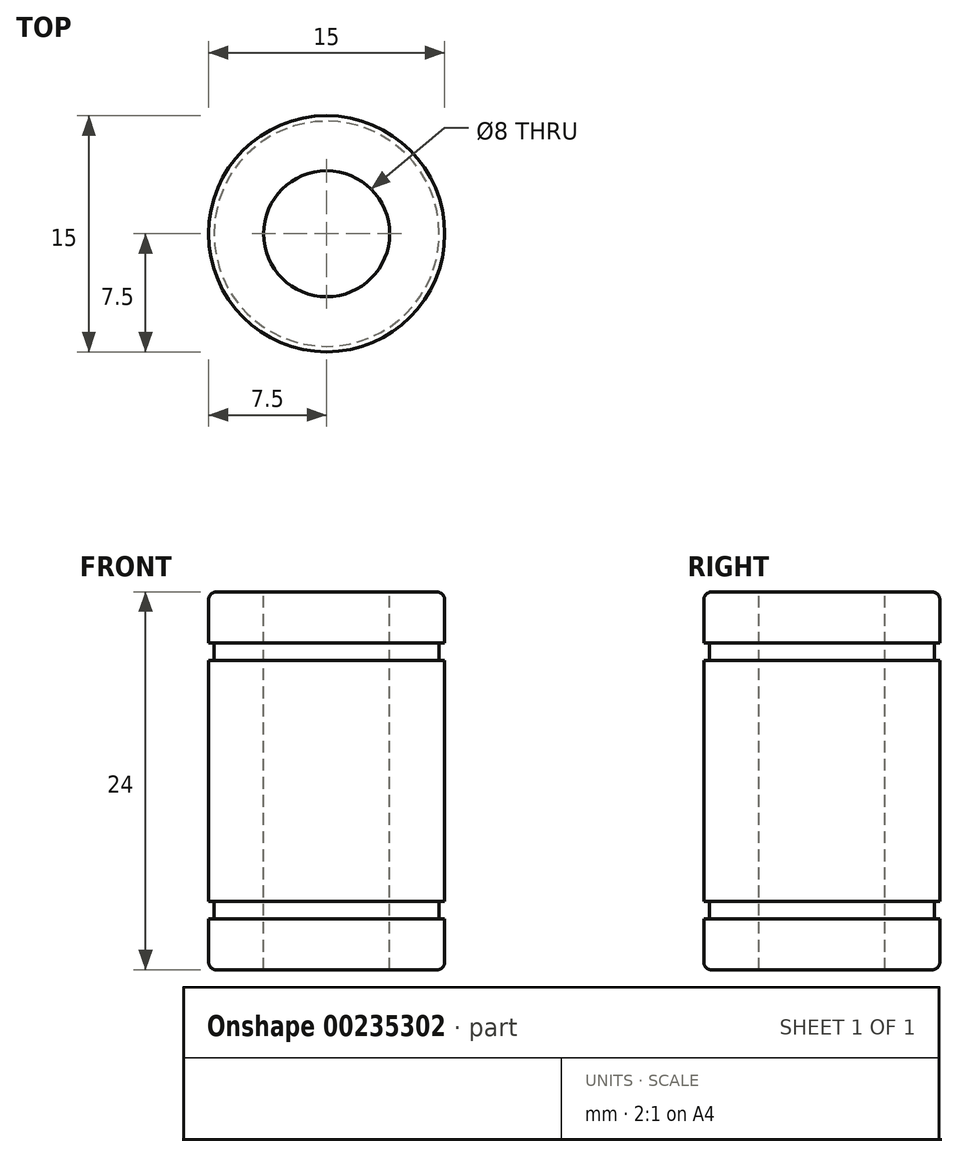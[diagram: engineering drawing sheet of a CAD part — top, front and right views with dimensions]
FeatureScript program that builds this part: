
annotation { "Feature Type Name" : "Feature", "Feature Type Description" : "" }
export const myFeature = defineFeature(function(context is Context, id is Id, definition is map)
    precondition{}
    {
        {
            var Q0;
            Q0=qCreatedBy(makeId("Front.planeOp"),FACE);
            var sketch = newSketch(context, id + "F0", { "sketchPlane" : qUnion([Q0])});
            skLineSegment(sketch, "E0", {"start": v(0, 0) * mm, "end": v(0, 24) * mm});
            skLineSegment(sketch, "E1", {"start": v(0, 24) * mm, "end": v(-7.5, 24) * mm});
            skLineSegment(sketch, "E2", {"start": v(-7.5, 24) * mm, "end": v(-7.5, 20.75) * mm});
            skLineSegment(sketch, "E3", {"start": v(-7.5, 20.75) * mm, "end": v(-7.15, 20.75) * mm});
            skLineSegment(sketch, "E4", {"start": v(-7.15, 20.75) * mm, "end": v(-7.15, 19.65) * mm});
            skLineSegment(sketch, "E5", {"start": v(-7.15, 19.65) * mm, "end": v(-7.5, 19.65) * mm});
            skLineSegment(sketch, "E6", {"start": v(-7.5, 3.25) * mm, "end": v(-7.15, 3.25) * mm});
            skLineSegment(sketch, "E7", {"start": v(-7.15, 4.35) * mm, "end": v(-7.15, 3.25) * mm});
            skLineSegment(sketch, "E8", {"start": v(-7.15, 4.35) * mm, "end": v(-7.5, 4.35) * mm});
            skLineSegment(sketch, "E9", {"start": v(-7.5, 0) * mm, "end": v(0, 0) * mm});
            skLineSegment(sketch, "E10", {"start": v(-7.5, 3.25) * mm, "end": v(-7.5, 0) * mm});
            skLineSegment(sketch, "E11", {"start": v(-7.5, 19.65) * mm, "end": v(-7.5, 4.35) * mm});
            skSolve(sketch);
        }
        {
            var Q0;
            Q0=makeQuery(id+"F0.imprint","IMPRINT",FACE,{"disambiguationData":[TD([[makeQuery(id+"F0.imprint","IMPRINT",EDGE,{"derivedFrom":sQuery(id+"F0.wireOp",EDGE,"E0")}),1.0]])]});
            var Q1;
            Q1=sQuery(id+"F0.wireOp",EDGE,"E0");
            revolve(context, id + "F1", {"entities" : qUnion([Q0]), "axis" : qUnion([Q1]), "revolveType" : RevolveType.FULL});
        }
        {
            var Q0;
            Q0=makeQuery(id+"F1.opRevolve","SWEPT_FACE",FACE,{"disambiguationData":[OSD([sQuery(id+"F0.wireOp",EDGE,"E1")])]});
            var sketch = newSketch(context, id + "F2", { "sketchPlane" : qUnion([Q0])});
            skCircle(sketch, "E12", {"center": v(0, 0) * mm, "radius": 4 * mm});
            skSolve(sketch);
        }
        {
            var Q0;
            Q0=qSketchRegion(id+"F2",true);
            extrude(context, id + "F3", {"entities" : qUnion([Q0]), "operationType" : NewBodyOperationType.REMOVE, "oppositeDirection" : true, "depth" : 25 * mm});
        }
        {
            var Q0;
            Q0=makeQuery(id+"F1.opRevolve","SWEPT_EDGE",EDGE,{"disambiguationData":[OSD([sQuery(id+"F0.wireOp",EDGE,"E9"),sQuery(id+"F0.wireOp",EDGE,"E10")])]});
            var Q1;
            Q1=makeQuery(id+"F1.opRevolve","SWEPT_EDGE",EDGE,{"disambiguationData":[OSD([sQuery(id+"F0.wireOp",EDGE,"E1"),sQuery(id+"F0.wireOp",EDGE,"E2")])]});
            fillet(context, id + "F4", {"entities" : qUnion([Q0, Q1]), "radius" : .5 * mm, "tangentPropagation" : true, "allowEdgeOverflow" : false});
        }
    });
